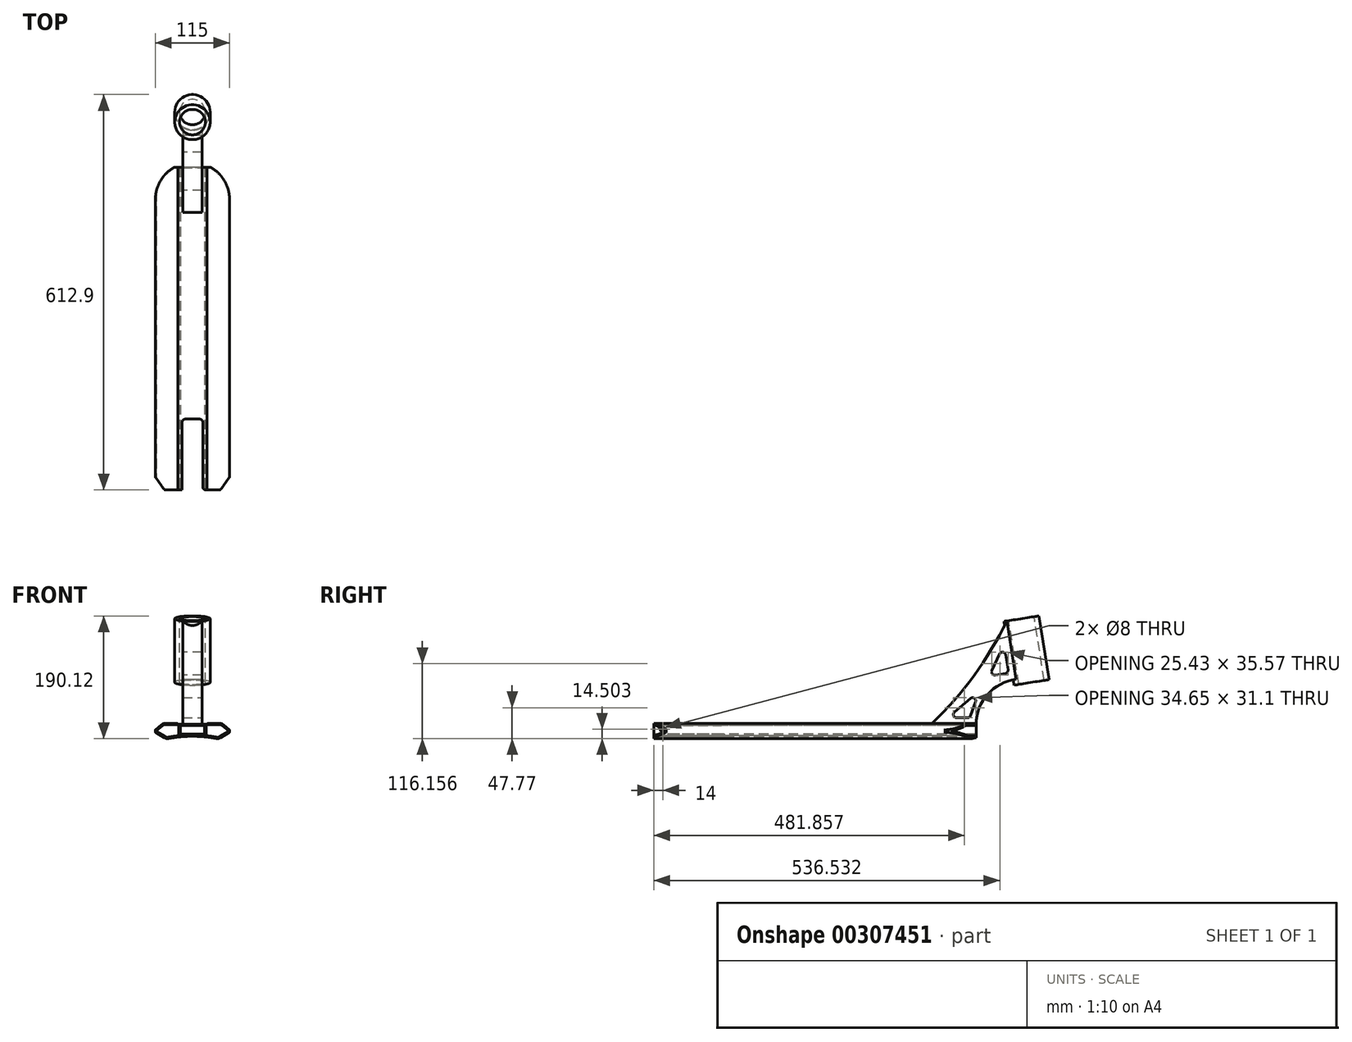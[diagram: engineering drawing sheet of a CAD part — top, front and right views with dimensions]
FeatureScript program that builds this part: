
annotation { "Feature Type Name" : "Feature", "Feature Type Description" : "" }
export const myFeature = defineFeature(function(context is Context, id is Id, definition is map)
    precondition{}
    {
        {
            var Q0;
            Q0=qCreatedBy(makeId("Front.planeOp"),FACE);
            var sketch = newSketch(context, id + "F0", { "sketchPlane" : qUnion([Q0])});
            skLineSegment(sketch, "E0", {"start": v(0, 0) * mm, "end": v(0, 0) * mm});
            skLineSegment(sketch, "E1", {"start": v(0, 0) * mm, "end": v(22.5, 0) * mm});
            skPoint(sketch, "E1.endSnap0", {"position": v(0, 0) * mm});
            skLineSegment(sketch, "E2", {"start": v(22.5, 0) * mm, "end": v(22.5, 1.3) * mm});
            skLineSegment(sketch, "E3", {"start": v(22.5, 1.3) * mm, "end": v(45.58, 1.3) * mm});
            skLineSegment(sketch, "E4", {"start": v(45.58, 1.3) * mm, "end": v(57.5, -8.7) * mm});
            skLineSegment(sketch, "E5", {"start": v(57.5, -8.7) * mm, "end": v(57.5, -12.7) * mm});
            skLineSegment(sketch, "E6", {"start": v(57.5, -12.7) * mm, "end": v(40.18, -22.7) * mm});
            skLineSegment(sketch, "E7.MirrorCS", {"start": v(-57.5, -12.7) * mm, "end": v(-40.18, -22.7) * mm});
            skLineSegment(sketch, "E8.MirrorCS", {"start": v(-57.5, -8.7) * mm, "end": v(-57.5, -12.7) * mm});
            skLineSegment(sketch, "E9.MirrorCS", {"start": v(-45.58, 1.3) * mm, "end": v(-57.5, -8.7) * mm});
            skLineSegment(sketch, "E10.MirrorCS", {"start": v(-22.5, 0) * mm, "end": v(-22.5, 1.3) * mm});
            skLineSegment(sketch, "E11.MirrorCS", {"start": v(0, 0) * mm, "end": v(-22.5, 0) * mm});
            skLineSegment(sketch, "E12.MirrorCS", {"start": v(-22.5, 1.3) * mm, "end": v(-45.58, 1.3) * mm});
            skArc(sketch, "E13", {"start": v(40.18, -22.7) * mm, "mid": v(0, -18.62) * mm, "end": v(-40.18, -22.7) * mm});
            skSolve(sketch);
        }
        {
            var Q0;
            Q0 = qSketchRegion(id + "F0", true);
            extrude(context, id + "F1", {"entities" : qUnion([Q0]), "endBound" : BoundingType.SYMMETRIC, "depth" : 500 * mm});
        }
        {
            var Q0;
            Q0=qCreatedBy(makeId("Front.planeOp"),FACE);
            var sketch = newSketch(context, id + "F2", { "sketchPlane" : qUnion([Q0])});
            skLineSegment(sketch, "E14.bottom", {"start": v(-19, -2) * mm, "end": v(19, -2) * mm});
            skLineSegment(sketch, "E14.top", {"start": v(-19, -15) * mm, "end": v(19, -15) * mm});
            skLineSegment(sketch, "E14.left", {"start": v(-19, -2) * mm, "end": v(-19, -15) * mm});
            skLineSegment(sketch, "E14.right", {"start": v(19, -2) * mm, "end": v(19, -15) * mm});
            skSolve(sketch);
        }
        {
            var Q0;
            Q0 = qSketchRegion(id + "F2", true);
            extrude(context, id + "F3", {"entities" : qUnion([Q0]), "operationType" : NewBodyOperationType.REMOVE, "endBound" : BoundingType.SYMMETRIC, "oppositeDirection" : true, "depth" : 500 * mm});
        }
        {
            var Q0;
            Q0=makeQuery(id+"F1.opExtrude","CAP_FACE",FACE,{"disambiguationData":[OSD([sQuery(id+"F0.wireOp",EDGE,"E1"),sQuery(id+"F0.wireOp",EDGE,"E2"),sQuery(id+"F0.wireOp",EDGE,"E3"),sQuery(id+"F0.wireOp",EDGE,"E4"),sQuery(id+"F0.wireOp",EDGE,"E5"),sQuery(id+"F0.wireOp",EDGE,"E6"),sQuery(id+"F0.wireOp",EDGE,"E7.MirrorCS"),sQuery(id+"F0.wireOp",EDGE,"E8.MirrorCS"),sQuery(id+"F0.wireOp",EDGE,"E9.MirrorCS"),sQuery(id+"F0.wireOp",EDGE,"E10.MirrorCS"),sQuery(id+"F0.wireOp",EDGE,"E11.MirrorCS"),sQuery(id+"F0.wireOp",EDGE,"E12.MirrorCS"),sQuery(id+"F0.wireOp",EDGE,"E13")])],"isStart":false});
            var sketch = newSketch(context, id + "F4", { "sketchPlane" : qUnion([Q0])});
            skLineSegment(sketch, "E15.0.0", {"start": v(-48.1, -0.8) * mm, "end": v(-57.14, -8.4) * mm});
            skArc(sketch, "E15.0.1", {"start": v(-57.14, -8.4) * mm, "mid": v(-57.4, -8.74) * mm, "end": v(-57.5, -9.17) * mm});
            skLineSegment(sketch, "E15.0.2", {"start": v(-57.5, -9.17) * mm, "end": v(-57.5, -12.12) * mm});
            skArc(sketch, "E15.0.3", {"start": v(-57.5, -12.12) * mm, "mid": v(-57.37, -12.62) * mm, "end": v(-57, -12.99) * mm});
            skLineSegment(sketch, "E15.0.4", {"start": v(-57, -12.99) * mm, "end": v(-43.1, -21.01) * mm});
            skArc(sketch, "E15.0.5", {"start": v(-43.1, -21.01) * mm, "mid": v(-40.12, -22.1) * mm, "end": v(-36.94, -22.06) * mm});
            skArc(sketch, "E15.0.6", {"start": v(-36.94, -22.06) * mm, "mid": v(0, -18.62) * mm, "end": v(36.94, -22.06) * mm});
            skArc(sketch, "E15.0.7", {"start": v(36.94, -22.06) * mm, "mid": v(40.12, -22.1) * mm, "end": v(43.1, -21.01) * mm});
            skLineSegment(sketch, "E15.0.8", {"start": v(43.1, -21.01) * mm, "end": v(57, -12.99) * mm});
            skArc(sketch, "E15.0.9", {"start": v(57, -12.99) * mm, "mid": v(57.37, -12.62) * mm, "end": v(57.5, -12.12) * mm});
            skLineSegment(sketch, "E15.0.10", {"start": v(57.5, -12.12) * mm, "end": v(57.5, -9.17) * mm});
            skArc(sketch, "E15.0.11", {"start": v(57.5, -9.17) * mm, "mid": v(57.4, -8.74) * mm, "end": v(57.14, -8.4) * mm});
            skLineSegment(sketch, "E15.0.12", {"start": v(57.14, -8.4) * mm, "end": v(48.1, -0.8) * mm});
            skArc(sketch, "E15.0.13", {"start": v(48.1, -0.8) * mm, "mid": v(45.38, 0.76) * mm, "end": v(42.3, 1.3) * mm});
            skLineSegment(sketch, "E15.0.14", {"start": v(42.3, 1.3) * mm, "end": v(24.37, 1.3) * mm});
            skArc(sketch, "E15.0.15", {"start": v(24.37, 1.3) * mm, "mid": v(23.23, 0.94) * mm, "end": v(22.5, 0) * mm});
            skLineSegment(sketch, "E15.0.16", {"start": v(22.5, 0) * mm, "end": v(-22.5, 0) * mm});
            skArc(sketch, "E15.0.17", {"start": v(-22.5, 0) * mm, "mid": v(-23.23, 0.94) * mm, "end": v(-24.37, 1.3) * mm});
            skLineSegment(sketch, "E15.0.18", {"start": v(-24.37, 1.3) * mm, "end": v(-42.3, 1.3) * mm});
            skArc(sketch, "E15.0.19", {"start": v(-42.3, 1.3) * mm, "mid": v(-45.38, 0.76) * mm, "end": v(-48.1, -0.8) * mm});
            skLineSegment(sketch, "E16.0", {"start": v(-24.37, -0.7) * mm, "end": v(-42.3, -0.7) * mm});
            skArc(sketch, "E17.0", {"start": v(-37.3, -20.1) * mm, "mid": v(-29.18, -18.74) * mm, "end": v(-21, -17.72) * mm});
            skArc(sketch, "E17.1", {"start": v(-42.3, -0.7) * mm, "mid": v(-44.7, -1.12) * mm, "end": v(-46.8, -2.34) * mm});
            skLineSegment(sketch, "E17.2", {"start": v(-46.8, -2.34) * mm, "end": v(-55.76, -9.85) * mm});
            skLineSegment(sketch, "E17.3", {"start": v(-55.61, -11.48) * mm, "end": v(-42.1, -19.28) * mm});
            skArc(sketch, "E17.4", {"start": v(-42.1, -19.28) * mm, "mid": v(-39.78, -20.12) * mm, "end": v(-37.3, -20.1) * mm});
            skArc(sketch, "E18", {"start": v(-22.5, -2) * mm, "mid": v(-23.23, -1.06) * mm, "end": v(-24.37, -0.7) * mm});
            skPoint(sketch, "E19.visualSharp", {"position": v(-56.85, -10.77) * mm});
            skArc(sketch, "E19.filletArc", {"start": v(-55.76, -9.85) * mm, "mid": v(-56.1, -10.7) * mm, "end": v(-55.61, -11.48) * mm});
            skLineSegment(sketch, "E20", {"start": v(-22.5, -2) * mm, "end": v(-21, -2) * mm});
            skLineSegment(sketch, "E21", {"start": v(-21, -2) * mm, "end": v(-21, -17.72) * mm});
            skLineSegment(sketch, "E22.MirrorCS", {"start": v(21, -2) * mm, "end": v(21, -17.72) * mm});
            skArc(sketch, "E23.MirrorCS", {"start": v(37.3, -20.1) * mm, "mid": v(29.18, -18.74) * mm, "end": v(21, -17.72) * mm});
            skArc(sketch, "E24.MirrorCS", {"start": v(42.1, -19.28) * mm, "mid": v(39.78, -20.12) * mm, "end": v(37.3, -20.1) * mm});
            skLineSegment(sketch, "E25.MirrorCS", {"start": v(55.61, -11.48) * mm, "end": v(42.1, -19.28) * mm});
            skArc(sketch, "E26.MirrorCS", {"start": v(55.76, -9.85) * mm, "mid": v(56.1, -10.7) * mm, "end": v(55.61, -11.48) * mm});
            skLineSegment(sketch, "E27.MirrorCS", {"start": v(46.8, -2.34) * mm, "end": v(55.76, -9.85) * mm});
            skArc(sketch, "E28.MirrorCS", {"start": v(42.3, -0.7) * mm, "mid": v(44.7, -1.12) * mm, "end": v(46.8, -2.34) * mm});
            skLineSegment(sketch, "E29.MirrorCS", {"start": v(24.37, -0.7) * mm, "end": v(42.3, -0.7) * mm});
            skArc(sketch, "E30.MirrorCS", {"start": v(22.5, -2) * mm, "mid": v(23.23, -1.06) * mm, "end": v(24.37, -0.7) * mm});
            skLineSegment(sketch, "E31.MirrorCS", {"start": v(22.5, -2) * mm, "end": v(21, -2) * mm});
            skSolve(sketch);
        }
        {
            var Q0;
            Q0=makeQuery(id+"F1.opExtrude","SWEPT_EDGE",EDGE,{"disambiguationData":[OSD([sQuery(id+"F0.wireOp",EDGE,"E10.MirrorCS"),sQuery(id+"F0.wireOp",EDGE,"E12.MirrorCS")])]});
            var Q1;
            Q1=makeQuery(id+"F1.opExtrude","SWEPT_EDGE",EDGE,{"disambiguationData":[OSD([sQuery(id+"F0.wireOp",EDGE,"E2"),sQuery(id+"F0.wireOp",EDGE,"E3")])]});
            fillet(context, id + "F5", {"entities" : qUnion([Q0, Q1]), "radius" : 2 * mm, "tangentPropagation" : true, "allowEdgeOverflow" : false});
        }
        {
            var Q0;
            Q0=makeQuery(id+"F1.opExtrude","SWEPT_EDGE",EDGE,{"disambiguationData":[OSD([sQuery(id+"F0.wireOp",EDGE,"E7.MirrorCS"),sQuery(id+"F0.wireOp",EDGE,"E13")])]});
            var Q1;
            Q1=makeQuery(id+"F1.opExtrude","SWEPT_EDGE",EDGE,{"disambiguationData":[OSD([sQuery(id+"F0.wireOp",EDGE,"E9.MirrorCS"),sQuery(id+"F0.wireOp",EDGE,"E12.MirrorCS")])]});
            var Q2;
            Q2=makeQuery(id+"F1.opExtrude","SWEPT_EDGE",EDGE,{"disambiguationData":[OSD([sQuery(id+"F0.wireOp",EDGE,"E6"),sQuery(id+"F0.wireOp",EDGE,"E13")])]});
            var Q3;
            Q3=makeQuery(id+"F1.opExtrude","SWEPT_EDGE",EDGE,{"disambiguationData":[OSD([sQuery(id+"F0.wireOp",EDGE,"E3"),sQuery(id+"F0.wireOp",EDGE,"E4")])]});
            fillet(context, id + "F6", {"entities" : qUnion([Q0, Q1, Q2, Q3]), "radius" : 9 * mm, "tangentPropagation" : true, "allowEdgeOverflow" : false});
        }
        {
            var Q0;
            Q0=makeQuery(id+"F1.opExtrude","SWEPT_EDGE",EDGE,{"disambiguationData":[OSD([sQuery(id+"F0.wireOp",EDGE,"E8.MirrorCS"),sQuery(id+"F0.wireOp",EDGE,"E9.MirrorCS")])]});
            var Q1;
            Q1=makeQuery(id+"F1.opExtrude","SWEPT_EDGE",EDGE,{"disambiguationData":[OSD([sQuery(id+"F0.wireOp",EDGE,"E7.MirrorCS"),sQuery(id+"F0.wireOp",EDGE,"E8.MirrorCS")])]});
            var Q2;
            Q2=makeQuery(id+"F1.opExtrude","SWEPT_EDGE",EDGE,{"disambiguationData":[OSD([sQuery(id+"F0.wireOp",EDGE,"E4"),sQuery(id+"F0.wireOp",EDGE,"E5")])]});
            var Q3;
            Q3=makeQuery(id+"F1.opExtrude","SWEPT_EDGE",EDGE,{"disambiguationData":[OSD([sQuery(id+"F0.wireOp",EDGE,"E5"),sQuery(id+"F0.wireOp",EDGE,"E6")])]});
            fillet(context, id + "F7", {"entities" : qUnion([Q0, Q1, Q2, Q3]), "radius" : 1 * mm, "tangentPropagation" : true, "allowEdgeOverflow" : false});
        }
        {
            var Q0;
            Q0=makeQuery(id+"F4.imprint","IMPRINT",FACE,{"disambiguationData":[TD([[makeQuery(id+"F4.imprint","IMPRINT",EDGE,{"derivedFrom":sQuery(id+"F4.wireOp",EDGE,"E22.MirrorCS")}),1.0]])]});
            var Q1;
            Q1=makeQuery(id+"F4.imprint","IMPRINT",FACE,{"disambiguationData":[TD([[makeQuery(id+"F4.imprint","IMPRINT",EDGE,{"derivedFrom":sQuery(id+"F4.wireOp",EDGE,"E16.0")}),1.0]])]});
            extrude(context, id + "F8", {"entities" : qUnion([Q0, Q1]), "operationType" : NewBodyOperationType.REMOVE, "endBound" : BoundingType.THROUGH_ALL, "oppositeDirection" : true, "depth" : 25 * mm});
        }
        {
            var Q0;
            Q0=qCreatedBy(makeId("Top.planeOp"),FACE);
            var sketch = newSketch(context, id + "F9", { "sketchPlane" : qUnion([Q0])});
            skArc(sketch, "E32", {"start": v(57.5, 200) * mm, "mid": v(0, 257.5) * mm, "end": v(-57.5, 200) * mm});
            skLineSegment(sketch, "E33", {"start": v(-57.5, 200) * mm, "end": v(-57.5, 280) * mm});
            skLineSegment(sketch, "E34", {"start": v(-57.5, 280) * mm, "end": v(57.5, 280) * mm});
            skLineSegment(sketch, "E35", {"start": v(57.5, 280) * mm, "end": v(57.5, 200) * mm});
            skSolve(sketch);
        }
        {
            var Q0;
            Q0 = qSketchRegion(id + "F9", true);
            extrude(context, id + "F10", {"entities" : qUnion([Q0]), "operationType" : NewBodyOperationType.REMOVE, "endBound" : BoundingType.THROUGH_ALL, "oppositeDirection" : true, "depth" : 25 * mm, "hasSecondDirection" : true, "secondDirectionBound" : SecondDirectionBoundingType.THROUGH_ALL, "secondDirectionOppositeDirection" : false, "secondDirectionDepth" : 25 * mm});
        }
        {
            var Q0;
            Q0=qCreatedBy(makeId("Top.planeOp"),FACE);
            var sketch = newSketch(context, id + "F11", { "sketchPlane" : qUnion([Q0])});
            skLineSegment(sketch, "E36", {"start": v(-68, -216) * mm, "end": v(-68, -346) * mm});
            skLineSegment(sketch, "E37", {"start": v(-68, -346) * mm, "end": v(68, -346) * mm});
            skLineSegment(sketch, "E38", {"start": v(68, -346) * mm, "end": v(68, -216) * mm});
            skLineSegment(sketch, "E39", {"start": v(68, -216) * mm, "end": v(43.3, -250) * mm});
            skLineSegment(sketch, "E40", {"start": v(43.3, -250) * mm, "end": v(16, -250) * mm});
            skLineSegment(sketch, "E41", {"start": v(16, -250) * mm, "end": v(16, -140) * mm});
            skLineSegment(sketch, "E42", {"start": v(16, -140) * mm, "end": v(-16, -140) * mm});
            skLineSegment(sketch, "E43", {"start": v(-16, -140) * mm, "end": v(-16, -250) * mm});
            skLineSegment(sketch, "E44", {"start": v(-16, -250) * mm, "end": v(-43.3, -250) * mm});
            skLineSegment(sketch, "E45", {"start": v(-43.3, -250) * mm, "end": v(-68, -216) * mm});
            skSolve(sketch);
        }
        {
            var Q0;
            Q0 = qSketchRegion(id + "F11", true);
            extrude(context, id + "F12", {"entities" : qUnion([Q0]), "operationType" : NewBodyOperationType.REMOVE, "endBound" : BoundingType.THROUGH_ALL, "oppositeDirection" : true, "depth" : 25 * mm, "hasSecondDirection" : true, "secondDirectionBound" : SecondDirectionBoundingType.THROUGH_ALL, "secondDirectionOppositeDirection" : false, "secondDirectionDepth" : 25 * mm});
        }
        {
            var Q0;
            {var subQ0=sQuery(id+"F11.wireOp",EDGE,"E42");var subQ1=sQuery(id+"F11.wireOp",EDGE,"E43");Q0=makeQuery(id+"F12.boolean.opBoolean","COPY",EDGE,{"disambiguationData":[TD([makeQuery(id+"F3.boolean.opBoolean","COPY",FACE,{"derivedFrom":makeQuery(id+"F3.opExtrude","SWEPT_FACE",FACE,{"disambiguationData":[OSD([sQuery(id+"F2.wireOp",EDGE,"E14.bottom")])]})})])],"derivedFrom":makeQuery(id+"F12.opExtrude","SWEPT_EDGE",EDGE,{"disambiguationData":[OSD([subQ0,subQ1])]})});}
            var Q1;
            {var subQ0=sQuery(id+"F0.wireOp",EDGE,"E13");var subQ1=sQuery(id+"F11.wireOp",EDGE,"E43");Q1=makeQuery(id+"F12.boolean.opBoolean","COPY",EDGE,{"disambiguationData":[TD([makeQuery(id+"F1.opExtrude","SWEPT_FACE",FACE,{"disambiguationData":[OSD([subQ0])]})])],"derivedFrom":makeQuery(id+"F12.opExtrude","SWEPT_EDGE",EDGE,{"disambiguationData":[OSD([subQ1,sQuery(id+"F11.wireOp",EDGE,"E44")])]})});}
            var Q2;
            {var subQ2=sQuery(id+"F11.wireOp",EDGE,"E41");Q2=makeQuery(id+"F12.boolean.opBoolean","COPY",EDGE,{"disambiguationData":[TD([makeQuery(id+"F3.boolean.opBoolean","COPY",FACE,{"derivedFrom":makeQuery(id+"F3.opExtrude","SWEPT_FACE",FACE,{"disambiguationData":[OSD([sQuery(id+"F2.wireOp",EDGE,"E14.bottom")])]})})])],"derivedFrom":makeQuery(id+"F12.opExtrude","SWEPT_EDGE",EDGE,{"disambiguationData":[OSD([sQuery(id+"F11.wireOp",EDGE,"E40"),subQ2])]})});}
            var Q3;
            {var subQ0=sQuery(id+"F0.wireOp",EDGE,"E13");var subQ1=sQuery(id+"F11.wireOp",EDGE,"E41");Q3=makeQuery(id+"F12.boolean.opBoolean","COPY",EDGE,{"disambiguationData":[TD([makeQuery(id+"F1.opExtrude","SWEPT_FACE",FACE,{"disambiguationData":[OSD([subQ0])]})])],"derivedFrom":makeQuery(id+"F12.opExtrude","SWEPT_EDGE",EDGE,{"disambiguationData":[OSD([sQuery(id+"F11.wireOp",EDGE,"E40"),subQ1])]})});}
            var Q4;
            {var subQ0=sQuery(id+"F11.wireOp",EDGE,"E43");var subQ1=sQuery(id+"F11.wireOp",EDGE,"E42");Q4=makeQuery(id+"F12.boolean.opBoolean","COPY",EDGE,{"disambiguationData":[TD([makeQuery(id+"F1.opExtrude","SWEPT_FACE",FACE,{"disambiguationData":[OSD([sQuery(id+"F0.wireOp",EDGE,"E13")])]})])],"derivedFrom":makeQuery(id+"F12.opExtrude","SWEPT_EDGE",EDGE,{"disambiguationData":[OSD([subQ1,subQ0])]})});}
            var Q5;
            {var subQ0=sQuery(id+"F11.wireOp",EDGE,"E41");var subQ1=sQuery(id+"F11.wireOp",EDGE,"E42");Q5=makeQuery(id+"F12.boolean.opBoolean","COPY",EDGE,{"disambiguationData":[TD([makeQuery(id+"F1.opExtrude","SWEPT_FACE",FACE,{"disambiguationData":[OSD([sQuery(id+"F0.wireOp",EDGE,"E13")])]})])],"derivedFrom":makeQuery(id+"F12.opExtrude","SWEPT_EDGE",EDGE,{"disambiguationData":[OSD([subQ0,subQ1])]})});}
            var Q6;
            {var subQ0=sQuery(id+"F11.wireOp",EDGE,"E42");var subQ1=sQuery(id+"F11.wireOp",EDGE,"E41");Q6=makeQuery(id+"F12.boolean.opBoolean","COPY",EDGE,{"disambiguationData":[TD([makeQuery(id+"F3.boolean.opBoolean","COPY",FACE,{"derivedFrom":makeQuery(id+"F3.opExtrude","SWEPT_FACE",FACE,{"disambiguationData":[OSD([sQuery(id+"F2.wireOp",EDGE,"E14.bottom")])]})})])],"derivedFrom":makeQuery(id+"F12.opExtrude","SWEPT_EDGE",EDGE,{"disambiguationData":[OSD([subQ1,subQ0])]})});}
            fillet(context, id + "F13", {"entities" : qUnion([Q0, Q1, Q2, Q3, Q4, Q5, Q6]), "radius" : 5 * mm, "tangentPropagation" : true, "allowEdgeOverflow" : false});
        }
        {
            var Q0;
            Q0=qCreatedBy(makeId("Right.planeOp"),FACE);
            var sketch = newSketch(context, id + "F14", { "sketchPlane" : qUnion([Q0])});
            skLineSegment(sketch, "E46", {"start": v(180, 0) * mm, "end": v(250, 0) * mm});
            skArc(sketch, "E47", {"start": v(311.71, 69.5) * mm, "mid": v(267.66, 46.48) * mm, "end": v(250, 0) * mm});
            skLineSegment(sketch, "E48", {"start": v(311.71, 69.5) * mm, "end": v(313.03, 61.23) * mm});
            skLineSegment(sketch, "E49", {"start": v(313.03, 61.23) * mm, "end": v(358.46, 68.43) * mm});
            skLineSegment(sketch, "E50", {"start": v(358.46, 68.43) * mm, "end": v(342.82, 167.2) * mm});
            skLineSegment(sketch, "E51", {"start": v(342.82, 167.2) * mm, "end": v(297.38, 160) * mm});
            skArc(sketch, "E52", {"start": v(180, 0) * mm, "mid": v(245.97, 74.66) * mm, "end": v(297.38, 160) * mm});
            skSolve(sketch);
        }
        {
            var Q0;
            Q0 = qSketchRegion(id + "F14", true);
            extrude(context, id + "F15", {"entities" : qUnion([Q0]), "operationType" : NewBodyOperationType.ADD, "endBound" : BoundingType.SYMMETRIC, "depth" : 30 * mm});
        }
        {
            var Q0;
            Q0=makeQuery(id+"F15.opExtrude","SWEPT_FACE",FACE,{"disambiguationData":[OSD([sQuery(id+"F14.wireOp",EDGE,"E51")])]});
            var sketch = newSketch(context, id + "F16", { "sketchPlane" : qUnion([Q0])});
            skCircle(sketch, "E53", {"center": v(0, 341.75) * mm, "radius": 27.5 * mm});
            skSolve(sketch);
        }
        {
            var Q0;
            Q0 = qSketchRegion(id + "F16", true);
            var Q1;
            Q1=makeQuery(id+"F15.opExtrude","SWEPT_FACE",FACE,{"disambiguationData":[OSD([sQuery(id+"F14.wireOp",EDGE,"E49")])]});
            extrude(context, id + "F17", {"entities" : qUnion([Q0]), "operationType" : NewBodyOperationType.ADD, "endBound" : BoundingType.UP_TO_SURFACE, "oppositeDirection" : true, "endBoundEntityFace" : qUnion([Q1]), "depth" : 25 * mm});
        }
        {
            var Q0;
            Q0=makeQuery(id+"F17.boolean.opBoolean","MERGE",FACE,{"derivedFrom":[makeQuery(id+"F15.opExtrude","SWEPT_FACE",FACE,{"disambiguationData":[OSD([sQuery(id+"F14.wireOp",EDGE,"E51")])]}),makeQuery(id+"F17.opExtrude","CAP_FACE",FACE,{"disambiguationData":[OSD([sQuery(id+"F16.wireOp",EDGE,"E53")])],"isStart":true})]});
            var sketch = newSketch(context, id + "F18", { "sketchPlane" : qUnion([Q0])});
            skPoint(sketch, "E54", {"position": v(0, 341.75) * mm});
            skSolve(sketch);
        }
        {
            var Q0;
            Q0=sQuery(id+"F18.wireOp",VERTEX,"E54");
            var Q1;
            Q1=makeQuery(id+"F1.opExtrude","SWEPT_BODY",BODY,{"disambiguationData":[OSD([sQuery(id+"F0.wireOp",EDGE,"E1"),sQuery(id+"F0.wireOp",EDGE,"E2"),sQuery(id+"F0.wireOp",EDGE,"E3"),sQuery(id+"F0.wireOp",EDGE,"E4"),sQuery(id+"F0.wireOp",EDGE,"E5"),sQuery(id+"F0.wireOp",EDGE,"E6"),sQuery(id+"F0.wireOp",EDGE,"E7.MirrorCS"),sQuery(id+"F0.wireOp",EDGE,"E8.MirrorCS"),sQuery(id+"F0.wireOp",EDGE,"E9.MirrorCS"),sQuery(id+"F0.wireOp",EDGE,"E10.MirrorCS"),sQuery(id+"F0.wireOp",EDGE,"E11.MirrorCS"),sQuery(id+"F0.wireOp",EDGE,"E12.MirrorCS"),sQuery(id+"F0.wireOp",EDGE,"E13")])]});
            hole(context, id + "F19", {"style" : HoleStyle.SIMPLE, "endStyle" : HoleEndStyle.THROUGH, "holeDiameter" : 40 * mm, "isTappedThrough" : true, "tappedDepth" : 12 * mm, "tapClearance" : 3, "locations" : qUnion([Q0]), "scope" : qUnion([Q1])});
        }
        {
            var Q0;
            Q0=makeQuery(id+"F8.boolean.opBoolean","COPY",FACE,{"derivedFrom":makeQuery(id+"F8.opExtrude","SWEPT_FACE",FACE,{"disambiguationData":[OSD([sQuery(id+"F4.wireOp",EDGE,"E22.MirrorCS")])]})});
            var sketch = newSketch(context, id + "F20", { "sketchPlane" : qUnion([Q0])});
            skPoint(sketch, "E55", {"position": v(-236, -7.72) * mm});
            skSolve(sketch);
        }
        {
            var Q0;
            Q0=sQuery(id+"F20.wireOp",VERTEX,"E55");
            var Q1;
            Q1=makeQuery(id+"F1.opExtrude","SWEPT_BODY",BODY,{"disambiguationData":[OSD([sQuery(id+"F0.wireOp",EDGE,"E1"),sQuery(id+"F0.wireOp",EDGE,"E2"),sQuery(id+"F0.wireOp",EDGE,"E3"),sQuery(id+"F0.wireOp",EDGE,"E4"),sQuery(id+"F0.wireOp",EDGE,"E5"),sQuery(id+"F0.wireOp",EDGE,"E6"),sQuery(id+"F0.wireOp",EDGE,"E7.MirrorCS"),sQuery(id+"F0.wireOp",EDGE,"E8.MirrorCS"),sQuery(id+"F0.wireOp",EDGE,"E9.MirrorCS"),sQuery(id+"F0.wireOp",EDGE,"E10.MirrorCS"),sQuery(id+"F0.wireOp",EDGE,"E11.MirrorCS"),sQuery(id+"F0.wireOp",EDGE,"E12.MirrorCS"),sQuery(id+"F0.wireOp",EDGE,"E13")])]});
            hole(context, id + "F21", {"style" : HoleStyle.SIMPLE, "endStyle" : HoleEndStyle.BLIND, "holeDiameter" : 8 * mm, "holeDepth" : 50 * mm, "isTappedThrough" : true, "tappedDepth" : 12 * mm, "tapClearance" : 3, "locations" : qUnion([Q0]), "scope" : qUnion([Q1])});
        }
        {
            var Q0;
            Q0=makeQuery(id+"F15.opExtrude","CAP_FACE",FACE,{"disambiguationData":[OSD([sQuery(id+"F14.wireOp",EDGE,"E46"),sQuery(id+"F14.wireOp",EDGE,"E47"),sQuery(id+"F14.wireOp",EDGE,"E48"),sQuery(id+"F14.wireOp",EDGE,"E49"),sQuery(id+"F14.wireOp",EDGE,"E50"),sQuery(id+"F14.wireOp",EDGE,"E51"),sQuery(id+"F14.wireOp",EDGE,"E52")])],"isStart":false});
            var sketch = newSketch(context, id + "F22", { "sketchPlane" : qUnion([Q0])});
            skLineSegment(sketch, "E56", {"start": v(255.4, 52.29) * mm, "end": v(240, 10) * mm});
            skLineSegment(sketch, "E57", {"start": v(255.4, 52.29) * mm, "end": v(206, 10) * mm});
            skLineSegment(sketch, "E58", {"start": v(206, 10) * mm, "end": v(240, 10) * mm});
            skLineSegment(sketch, "E59", {"start": v(270.34, 74.72) * mm, "end": v(299.97, 79.41) * mm});
            skLineSegment(sketch, "E60", {"start": v(299.97, 79.41) * mm, "end": v(292.93, 123.86) * mm});
            skLineSegment(sketch, "E61", {"start": v(292.93, 123.86) * mm, "end": v(270.34, 74.72) * mm});
            skSolve(sketch);
        }
        {
            var Q0;
            Q0 = qSketchRegion(id + "F22", true);
            extrude(context, id + "F23", {"entities" : qUnion([Q0]), "operationType" : NewBodyOperationType.REMOVE, "endBound" : BoundingType.THROUGH_ALL, "oppositeDirection" : true, "depth" : 25 * mm});
        }
        {
            var Q0;
            Q0=makeQuery(id+"F23.boolean.opBoolean","COPY",EDGE,{"derivedFrom":makeQuery(id+"F23.opExtrude","SWEPT_EDGE",EDGE,{"disambiguationData":[OSD([sQuery(id+"F22.wireOp",EDGE,"E56"),sQuery(id+"F22.wireOp",EDGE,"E58")])]})});
            var Q1;
            Q1=makeQuery(id+"F23.boolean.opBoolean","COPY",EDGE,{"derivedFrom":makeQuery(id+"F23.opExtrude","SWEPT_EDGE",EDGE,{"disambiguationData":[OSD([sQuery(id+"F22.wireOp",EDGE,"E57"),sQuery(id+"F22.wireOp",EDGE,"E58")])]})});
            var Q2;
            Q2=makeQuery(id+"F23.boolean.opBoolean","COPY",EDGE,{"derivedFrom":makeQuery(id+"F23.opExtrude","SWEPT_EDGE",EDGE,{"disambiguationData":[OSD([sQuery(id+"F22.wireOp",EDGE,"E56"),sQuery(id+"F22.wireOp",EDGE,"E57")])]})});
            var Q3;
            Q3=makeQuery(id+"F23.boolean.opBoolean","COPY",EDGE,{"derivedFrom":makeQuery(id+"F23.opExtrude","SWEPT_EDGE",EDGE,{"disambiguationData":[OSD([sQuery(id+"F22.wireOp",EDGE,"E60"),sQuery(id+"F22.wireOp",EDGE,"E61")])]})});
            var Q4;
            Q4=makeQuery(id+"F23.boolean.opBoolean","COPY",EDGE,{"derivedFrom":makeQuery(id+"F23.opExtrude","SWEPT_EDGE",EDGE,{"disambiguationData":[OSD([sQuery(id+"F22.wireOp",EDGE,"E59"),sQuery(id+"F22.wireOp",EDGE,"E60")])]})});
            var Q5;
            Q5=makeQuery(id+"F23.boolean.opBoolean","COPY",EDGE,{"derivedFrom":makeQuery(id+"F23.opExtrude","SWEPT_EDGE",EDGE,{"disambiguationData":[OSD([sQuery(id+"F22.wireOp",EDGE,"E59"),sQuery(id+"F22.wireOp",EDGE,"E61")])]})});
            fillet(context, id + "F24", {"entities" : qUnion([Q0, Q1, Q2, Q3, Q4, Q5]), "radius" : 5 * mm, "tangentPropagation" : true, "allowEdgeOverflow" : false});
        }
    });
